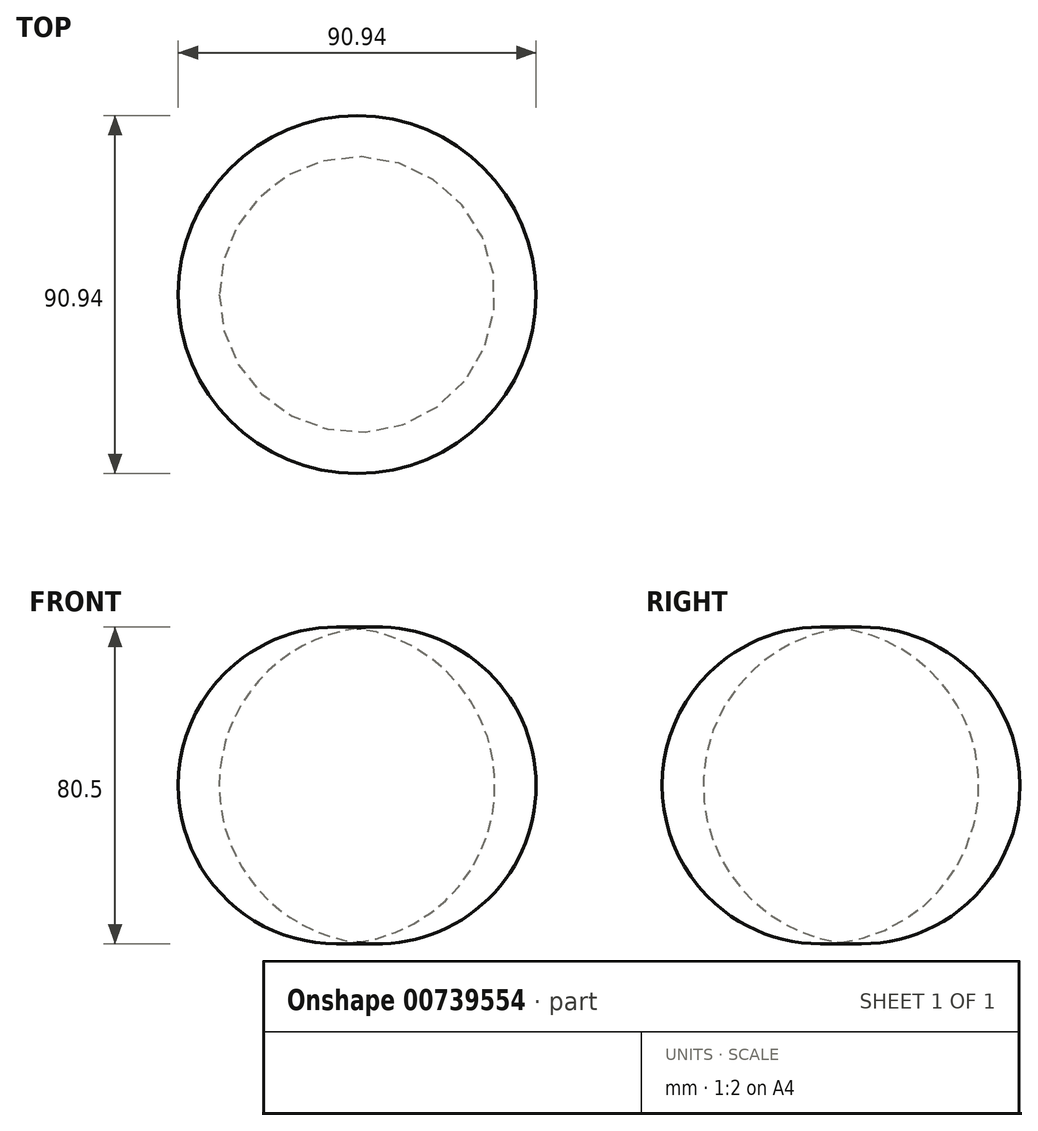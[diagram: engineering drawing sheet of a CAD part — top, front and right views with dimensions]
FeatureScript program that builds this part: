
annotation { "Feature Type Name" : "Feature", "Feature Type Description" : "" }
export const myFeature = defineFeature(function(context is Context, id is Id, definition is map)
    precondition{}
    {
        {
            var Q0;
            Q0=qCreatedBy(makeId("Front.planeOp"),FACE);
            var sketch = newSketch(context, id + "F0", { "sketchPlane" : qUnion([Q0])});
            skArc(sketch, "E0", {"start": v(0, -36.95) * mm, "mid": v(35.03, 2.96) * mm, "end": v(0, 42.87) * mm});
            skLineSegment(sketch, "E1", {"start": v(0, 42.87) * mm, "end": v(0, -36.95) * mm});
            skSolve(sketch);
        }
        {
            var Q0;
            Q0=makeQuery(id+"F0.imprint","IMPRINT",FACE,{"disambiguationData":[TD([[makeQuery(id+"F0.imprint","IMPRINT",EDGE,{"derivedFrom":sQuery(id+"F0.wireOp",EDGE,"E0")}),1.0]])]});
            var Q1;
            Q1=sQuery(id+"F0.wireOp",EDGE,"E1");
            revolve(context, id + "F1", {"surfaceOperationType" : NewSurfaceOperationType.NEW, "entities" : qUnion([Q0]), "axis" : qUnion([Q1]), "revolveType" : RevolveType.FULL});
        }
    });
